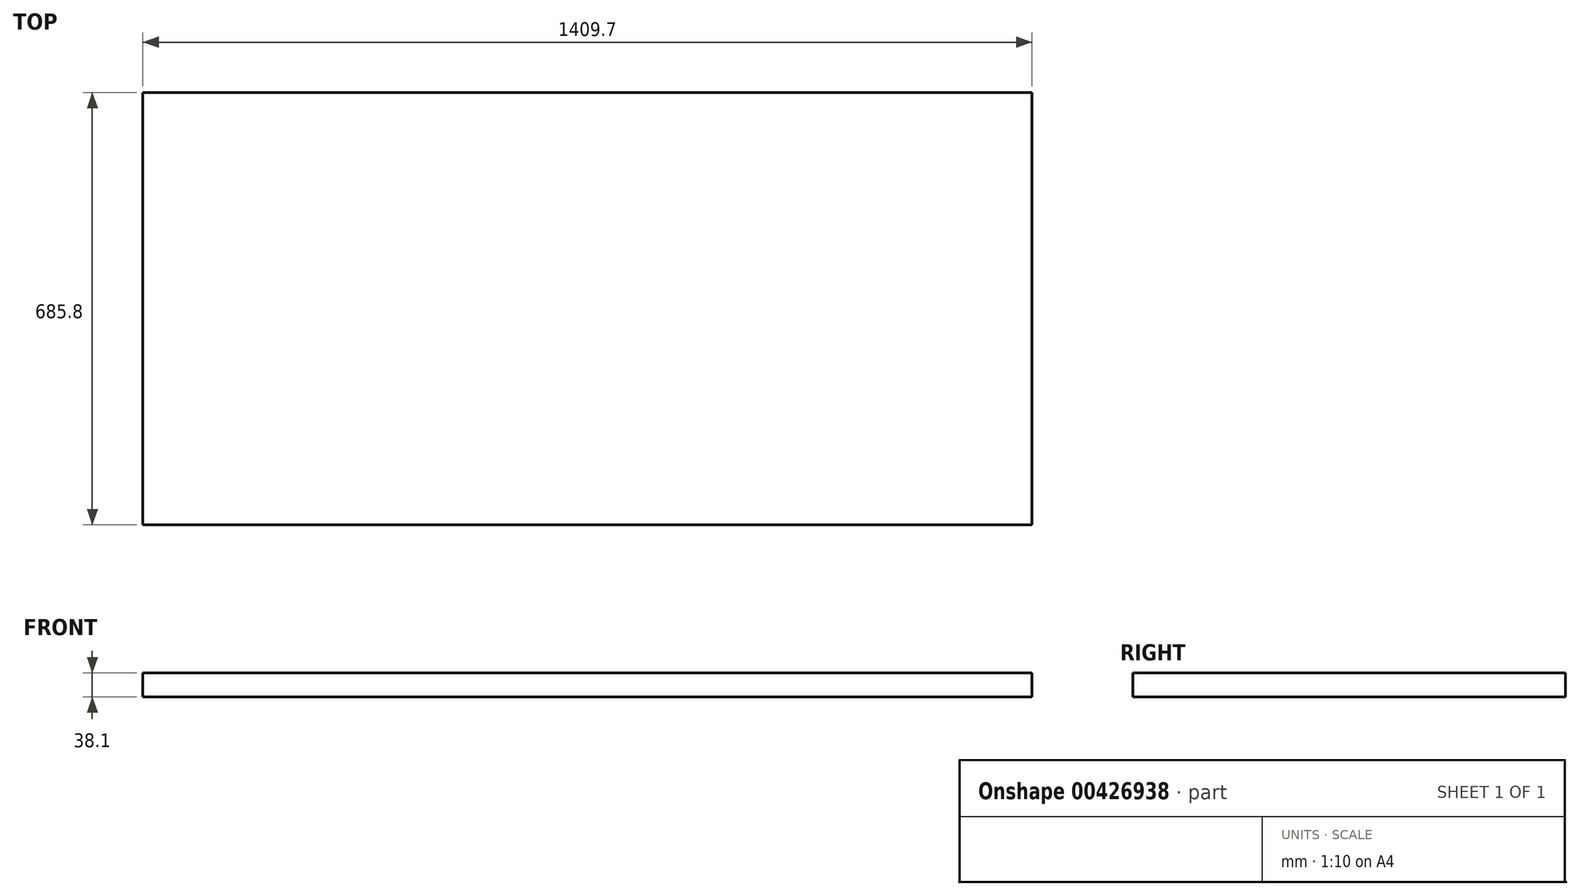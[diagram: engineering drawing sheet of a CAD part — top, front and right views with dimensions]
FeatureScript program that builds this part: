
annotation { "Feature Type Name" : "Feature", "Feature Type Description" : "" }
export const myFeature = defineFeature(function(context is Context, id is Id, definition is map)
    precondition{}
    {
        {
            var Q0;
            Q0=qCreatedBy(makeId("Top.planeOp"),FACE);
            var sketch = newSketch(context, id + "F0", { "sketchPlane" : qUnion([Q0])});
            skLineSegment(sketch, "E0", {"start": v(0, 0) * mm, "end": v(0, 685.8) * mm});
            skLineSegment(sketch, "E1", {"start": v(0, 685.8) * mm, "end": v(-1409.7, 685.8) * mm});
            skLineSegment(sketch, "E2", {"start": v(-1409.7, 685.8) * mm, "end": v(-1409.7, 0) * mm});
            skLineSegment(sketch, "E3", {"start": v(-1409.7, 0) * mm, "end": v(0, 0) * mm});
            skSolve(sketch);
        }
        {
            var Q0;
            Q0=makeQuery(id+"F0.imprint","IMPRINT",FACE,{"disambiguationData":[TD([[makeQuery(id+"F0.imprint","IMPRINT",EDGE,{"derivedFrom":sQuery(id+"F0.wireOp",EDGE,"E0")}),1.0]])]});
            extrude(context, id + "F1", {"entities" : qUnion([Q0]), "depth" : 38.1 * mm});
        }
    });
